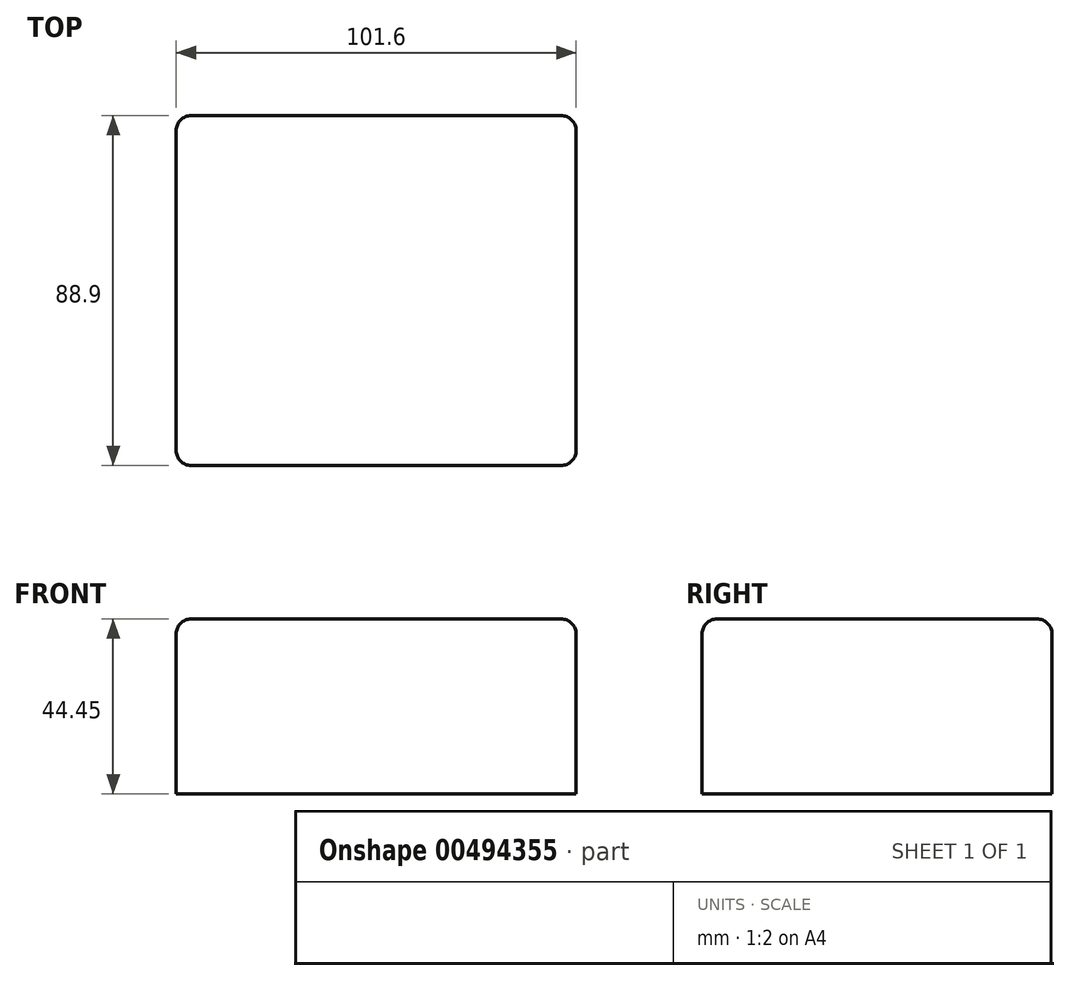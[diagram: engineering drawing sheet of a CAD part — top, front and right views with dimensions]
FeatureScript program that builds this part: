
annotation { "Feature Type Name" : "Feature", "Feature Type Description" : "" }
export const myFeature = defineFeature(function(context is Context, id is Id, definition is map)
    precondition{}
    {
        {
            var Q0;
            Q0=qCreatedBy(makeId("Top.planeOp"),FACE);
            var sketch = newSketch(context, id + "F0", { "sketchPlane" : qUnion([Q0])});
            skLineSegment(sketch, "E0.bottom", {"start": v(0, 0) * mm, "end": v(101.6, 0) * mm});
            skLineSegment(sketch, "E0.top", {"start": v(0, 88.9) * mm, "end": v(101.6, 88.9) * mm});
            skLineSegment(sketch, "E0.left", {"start": v(0, 0) * mm, "end": v(0, 88.9) * mm});
            skLineSegment(sketch, "E0.right", {"start": v(101.6, 0) * mm, "end": v(101.6, 88.9) * mm});
            skSolve(sketch);
        }
        {
            var Q0;
            Q0=makeQuery(id+"F0.imprint","IMPRINT",FACE,{"disambiguationData":[TD([[makeQuery(id+"F0.imprint","IMPRINT",EDGE,{"derivedFrom":sQuery(id+"F0.wireOp",EDGE,"E0.bottom")}),1.0]])]});
            extrude(context, id + "F1", {"entities" : qUnion([Q0]), "depth" : 44.45 * mm});
        }
        {
            var Q0;
            Q0=makeQuery(id+"F1.opExtrude","CAP_FACE",FACE,{"disambiguationData":[OSD([sQuery(id+"F0.wireOp",EDGE,"E0.bottom"),sQuery(id+"F0.wireOp",EDGE,"E0.top"),sQuery(id+"F0.wireOp",EDGE,"E0.left"),sQuery(id+"F0.wireOp",EDGE,"E0.right")])],"isStart":false});
            var Q1;
            Q1=makeQuery(id+"F1.opExtrude","SWEPT_EDGE",EDGE,{"disambiguationData":[OSD([sQuery(id+"F0.wireOp",EDGE,"E0.bottom"),sQuery(id+"F0.wireOp",EDGE,"E0.right")])]});
            var Q2;
            Q2=makeQuery(id+"F1.opExtrude","SWEPT_EDGE",EDGE,{"disambiguationData":[OSD([sQuery(id+"F0.wireOp",EDGE,"E0.top"),sQuery(id+"F0.wireOp",EDGE,"E0.right")])]});
            var Q3;
            Q3=makeQuery(id+"F1.opExtrude","SWEPT_EDGE",EDGE,{"disambiguationData":[OSD([sQuery(id+"F0.wireOp",EDGE,"E0.top"),sQuery(id+"F0.wireOp",EDGE,"E0.left")])]});
            var Q4;
            Q4=makeQuery(id+"F1.opExtrude","SWEPT_EDGE",EDGE,{"disambiguationData":[OSD([sQuery(id+"F0.wireOp",EDGE,"E0.bottom"),sQuery(id+"F0.wireOp",EDGE,"E0.left")])]});
            fillet(context, id + "F2", {"entities" : qUnion([Q0, Q1, Q2, Q3, Q4]), "radius" : 3.8 * mm, "tangentPropagation" : true, "allowEdgeOverflow" : false});
        }
    });
